# Revit family: JC KONTAKTER JCK277 Armbågskontakt
name_source: partatom
category: Specialty Equipment
units: mm (PartAtom-declared; Revit-internal decimal feet)

## family parameters
Always vertical = Yes
Cut with Voids When Loaded = No
Enable Cutting in Views = Yes
Host = Wall
Maintain Annotation Orientation = No
Part Type = Normal
Room Calculation Point = No
Round Connector Dimension = Use Diameter
Shared = No

## types (1)
- Armbågskontakt JCK277
    Antal mikrobrytare = 1
    CE Dokument = https://jckontakter.se
    Core Finish = Aluminum ENAW 6060
    Default Elevation = 0 mm  [stored 0 ft]
    Description = JCK277 är en modern modell utrustad med vägledande LED-ljus(blå). Modellen har även en nedsänkt taktil rilla för att underlätta användande för synnedsatta. Tillverkad i svarteloxerad aluminium med svarta endcaps.
    End Cap Finish = POM Tenac C 4520
    Lens Finish = Akryl
    Lid Finish = Aluminum ENAW 6060 (Svart)
    Lägsta märkström = 1mA/4 V DC
    Manufacturer = JC Kontakter
    Microbrytare = Standard NO/NC IP67 (tre ledare)
    Model = JCK277
    Nominell märkström = 12 V - Resistive 6A Inductive L/R 5ms 6A, 24 V - Resistive 6A Inductive L/R 5ms 5A
    Placering av armbågskontakt = https://jckontakter.se
    Produktvikt = 0.302 kg
    Tekniskt produktblad = https://jckontakter.se
    Tillvalsförteckning = https://jckontakter.se
    Tillverkningsland = Sverige
    URL = https://jckontakter.se

note: [stored X ft] marks values corroborated as IEEE doubles in the binary element streams (Revit-internal decimal feet)

## geometry (parser evidence)
native form markers: Sweep x9
no freeform markers — native parametric forms only
